# Revit family: Zumtobel ONLITE BRI
name_source: partatom
category: Lighting Fixtures
revit_build: Autodesk Revit 2016 (Build: 20150220_1215(x64)
units: mm (PartAtom-declared; Revit-internal decimal feet)

## family parameters
Always vertical = Yes
Cut with Voids When Loaded = No
Light Source = No
Part Type = Normal
Room Calculation Point = No
Round Connector Dimension = Use Diameter
Shared = No
Work Plane-Based = No

## types (1)
- ONLITE BRI
    Apparent Load = 0 VA
    Body = ZG_Metal_White
    Depth = 30 mm  [stored 0.0984252 ft]
    Description = Remote display for centrally supplied systems
    Height = 80 mm  [stored 0.262467 ft]
    Manufacturer = Zumtobel Lighting
    Model = 22185300
    URL = http://www.zumtobel.com
    Voltage = 0 V
    Width = 80 mm  [stored 0.262467 ft]

note: [stored X ft] marks values corroborated as IEEE doubles in the binary element streams (Revit-internal decimal feet)

## geometry (parser evidence)
native form markers: Sweep x3
no freeform markers — native parametric forms only
